# Revit family: LAMP_KOMBIC 150 ROUND IP40 OPTIC
name_source: partatom
category: Luminarias
revit_build: Autodesk Revit 2018 (Build: 20190510_1515(x64)
units: mm (PartAtom-declared; Revit-internal decimal feet)

## family parameters
Anfitrión = Cara
Compartido = No
Corte con vacíos al cargar = No
Cota de conector redondo = Diámetro de uso
Origen de luz = Sí
Punto de cálculo de habitación = No
Tipo de pieza = Normal

## types (24) — shared parameters
CRI = 80
Cambio de temperatura de color de luz atenuada = <Ninguno>
Diameter = 150 mm
Elevación por defecto = 1219 mm
Filtro de color = 16777215
Height = 100 mm  [stored 0.328084 ft]
IEE = A+
Insulation class = II
Lamp = COB LED
Luminaire type = Downlight
MacAdam = 3
Material COB = LAMP_COB
Material difusor = LAMP_PMMA Difusor Kombic
Material disipador = LAMP_Aluminio Disipador Kombic
Material optica = LAMP_PMMA Optica Kombic100
Power Supply = 220-240V 50/60Hz
Protection rating = IP40
Recessed diameter = 145 mm  [stored 0.475722 ft]
Type = COB PHILIPS
Weight = 0.69 kg
Ángulo de inclinación = -90.00°

## per-type parameters (varying)
| type | Archivo de red fotométrica | Efficacy | Fabricante | Finish | Gear | Installation instructions | LED Lifetime | Last update | Manufacturer URL | Manufacturer country | Manufacturer name | Material aro | Material reflector | Modelo | Plum | Power | Product URL | Product code | Product datasheet | UGR |
| 1145LM 3000K  B/B | K21RD2040WF830NBB.IES | 86 lm/W | LAMP | Matte black RAL 9011 | Electronic | https://www.lamp.es | 50.000 L90 B10 | 26/08/2021 | http://www.lamp.es | Spain | LAMP | LAMP_Plástico genérico NG | LAMP_PC Reflector Kombic Metalizado Negro | K21RD2040WF830NBB | 13 W | 12 W | https://www.lamp.es | K21RD2040WF830NBB | http://www.lamp.es | 16 |
| 1145LM 3000K  B/W | K21RD2040WF830NBW.IES | 86 lm/W | LAMP | Shiny white RAL 9010 | Electronic | https://www.lamp.es | 50.000 L90 B10 | 26/08/2021 | http://www.lamp.es | Spain | LAMP | LAMP_Plástico genérico BL | LAMP_PC Reflector Kombic Metalizado Negro | K21RD2040WF830NBW | 13 W | 12 W | https://www.lamp.es | K21RD2040WF830NBW | http://www.lamp.es | 16 |
| 1148LM 3000K  M/W | K21RD2040WF830NMW.IES | 86 lm/W | LAMP | Shiny white RAL 9010 | Electronic | https://www.lamp.es | 50.000 L90 B10 | 26/08/2021 | http://www.lamp.es | Spain | LAMP | LAMP_Plástico genérico BL | LAMP_PC Reflector Kombic Metalizado Mate | K21RD2040WF830NMW | 13 W | 12 W | https://www.lamp.es | K21RD2040WF830NMW | http://www.lamp.es | 16 |
| 1184LM 3000K  W/W | K21RD2040WF830NWW.IES | 88 lm/W | LAMP | Matte white RAL 9010 | Electronic | https://www.lamp.es | 50.000 L90 B10 | 26/08/2021 | http://www.lamp.es | Spain | LAMP | LAMP_Plástico genérico BL | LAMP_PC Reflector Kombic Blanco | K21RD2040WF830NWW | 13 W | 12 W | https://www.lamp.es | K21RD2040WF830NWW | http://www.lamp.es | 16 |
| 1193LM 4000K  B/B | K21RD2040WF840NBB.IES | 87 lm/W | LAMP | Matte black RAL 9011 | Electronic | https://www.lamp.es | 50.000 L90 B10 | 26/08/2021 | http://www.lamp.es | Spain | LAMP | LAMP_Plástico genérico NG | LAMP_PC Reflector Kombic Metalizado Negro | K21RD2040WF840NBB | 14 W | 12 W | https://www.lamp.es | K21RD2040WF840NBB | http://www.lamp.es | 16 |
| 1193LM 4000K  B/W | K21RD2040WF840NBW.IES | 87 lm/W | LAMP | Shiny white RAL 9010 | Electronic | https://www.lamp.es | 50.000 L90 B10 | 26/08/2021 | http://www.lamp.es | Spain | LAMP | LAMP_Plástico genérico BL | LAMP_PC Reflector Kombic Metalizado Negro | K21RD2040WF840NBW | 14 W | 12 W | https://www.lamp.es | K21RD2040WF840NBW | http://www.lamp.es | 16 |
| 1196LM 4000K  M/W | K21RD2040WF840NMW.IES | 87 lm/W | LAMP | Shiny white RAL 9010 | Electronic | https://www.lamp.es | 50.000 L90 B10 | 26/08/2021 | http://www.lamp.es | Spain | LAMP | LAMP_Plástico genérico BL | LAMP_PC Reflector Kombic Metalizado Mate | K21RD2040WF840NMW | 14 W | 12 W | https://www.lamp.es | K21RD2040WF840NMW | http://www.lamp.es | 16 |
| 1233LM 4000K  W/W | K21RD2040WF840NWW.IES | 90 lm/W | LAMP | Matte white RAL 9010 | Electronic | https://www.lamp.es | 50.000 L90 B10 | 26/08/2021 | http://www.lamp.es | Spain | LAMP | LAMP_Plástico genérico BL | LAMP_PC Reflector Kombic Blanco | K21RD2040WF840NWW | 14 W | 12 W | https://www.lamp.es | K21RD2040WF840NWW | http://www.lamp.es | 16 |
| 1613LM 3000K  B/B | K21RD3040WF830NBB.IES | 81 lm/W | LAMP | Matte black RAL 9011 | Electronic | https://www.lamp.es | 50.000 L70 B10 | 26/08/2021 | http://www.lamp.es | Spain | LAMP | LAMP_Plástico genérico NG | LAMP_PC Reflector Kombic Metalizado Negro | K21RD3040WF830NBB | 20 W | 18 W | https://www.lamp.es | K21RD3040WF830NBB | http://www.lamp.es | 19 |
| 1613LM 3000K  B/W | K21RD3040WF830NBW.IES | 81 lm/W | LAMP | Shiny white RAL 9010 | Electronic | https://www.lamp.es | 50.000 L70 B10 | 26/08/2021 | http://www.lamp.es | Spain | LAMP | LAMP_Plástico genérico BL | LAMP_PC Reflector Kombic Metalizado Negro | K21RD3040WF830NBW | 20 W | 18 W | https://www.lamp.es | K21RD3040WF830NBW | http://www.lamp.es | 19 |
| 1618LM 3000K  M/W | K21RD3040WF830NMW.IES | 81 lm/W | LAMP | Shiny white RAL 9010 | Electronic | https://www.lamp.es | 50.000 L70 B10 | 26/08/2021 | http://www.lamp.es | Spain | LAMP | LAMP_Plástico genérico BL | LAMP_PC Reflector Kombic Metalizado Mate | K21RD3040WF830NMW | 20 W | 18 W | https://www.lamp.es | K21RD3040WF830NMW | http://www.lamp.es | 19 |
| 1667LM 3000K  W/W | K21RD3040WF830NWW.IES | 84 lm/W | LAMP | Matte white RAL 9010 | Electronic | https://www.lamp.es | 50.000 L70 B10 | 26/08/2021 | http://www.lamp.es | Spain | LAMP | LAMP_Plástico genérico BL | LAMP_PC Reflector Kombic Blanco | K21RD3040WF830NWW | 20 W | 18 W | https://www.lamp.es | K21RD3040WF830NWW | http://www.lamp.es | 19 |
| 1680LM 4000K  B/B | K21RD3040WF840NBB.IES | 84 lm/W | LAMP | Matte black RAL 9011 | Electronic | https://www.lamp.es | 50.000 L70 B10 | 26/08/2021 | http://www.lamp.es | Spain | LAMP | LAMP_Plástico genérico NG | LAMP_PC Reflector Kombic Metalizado Negro | K21RD3040WF840NBB | 20 W | 18 W | https://www.lamp.es | K21RD3040WF840NBB | http://www.lamp.es | 19 |
| 1680LM 4000K  B/W | K21RD3040WF840NBW.IES | 84 lm/W | LAMP | Shiny white RAL 9010 | Electronic | https://www.lamp.es | 50.000 L70 B10 | 26/08/2021 | http://www.lamp.es | Spain | LAMP | LAMP_Plástico genérico BL | LAMP_PC Reflector Kombic Metalizado Negro | K21RD3040WF840NBW | 20 W | 18 W | https://www.lamp.es | K21RD3040WF840NBW | http://www.lamp.es | 19 |
| 1685LM 4000K  M/W | K21RD3040WF840NMW.IES | 87 lm/W | LAMP | Shiny white RAL 9010 | Electronic | https://www.lamp.es | 50.000 L70 B10 | 26/08/2021 | http://www.lamp.es | Spain | LAMP | LAMP_Plástico genérico BL | LAMP_PC Reflector Kombic Metalizado Mate | K21RD3040WF840NMW | 20 W | 18 W | https://www.lamp.es | K21RD3040WF840NMW | http://www.lamp.es | 19 |
| 1737LM 4000K  W/W | K21RD3040WF840NWW.IES | 91 lm/W | LAMP | Matte white RAL 9010 | Electronic | https://www.lamp.es | 50.000 L70 B10 | 26/08/2021 | http://www.lamp.es | Spain | LAMP | LAMP_Plástico genérico BL | LAMP_PC Reflector Kombic Blanco | K21RD3040WF840NWW | 19 W | 19 W | https://www.lamp.es | K21RD3040WF840NWW | http://www.lamp.es | 19 |
| 2145LM 3000K  B/B | K21RD3540WF830NBB.IES | 77 lm/W |  | Matte black RAL 9011 |  |  | 50.000 L70 B10 |  |  |  |  | LAMP_Plástico genérico NG | LAMP_PC Reflector Kombic Metalizado Negro | K21RD3540WF830NBB | 28 W | 25 W |  | K21RD3540WF830NBB |  | 19 |
| 2145LM 3000K  B/W | K21RD3540WF830NBW.IES | 77 lm/W |  | Shiny white RAL 9010 |  |  | 50.000 L70 B10 |  |  |  |  | LAMP_Plástico genérico BL | LAMP_PC Reflector Kombic Metalizado Negro | K21RD3540WF830NBW | 28 W | 25 W |  | K21RD3540WF830NBW |  | 19 |
| 2151LM 3000K  M/W | K21RD3540WF830NMW.IES | 78 lm/W |  | Shiny white RAL 9010 |  |  | 50.000 L70 B10 |  |  |  |  | LAMP_Plástico genérico BL | LAMP_PC Reflector Kombic Metalizado Mate | K21RD3540WF830NMW | 28 W | 25 W |  | K21RD3540WF830NMW |  | 19 |
| 2217LM 3000K  W/W | K21RD3540WF830NWW.IES | 80 lm/W |  | Matte white RAL 9010 |  |  | 50.000 L70 B10 |  |  |  |  | LAMP_Plástico genérico BL | LAMP_PC Reflector Kombic Blanco | K21RD3540WF830NWW | 28 W | 25 W |  | K21RD3540WF830NWW |  | 19 |
| 2235LM 4000K  B/B | K21RD3540WF840NBB.IES | 81 lm/W |  | Matte black RAL 9011 |  |  | 50.000 L70 B10 |  |  |  |  | LAMP_Plástico genérico NG | LAMP_PC Reflector Kombic Metalizado Negro | K21RD3540WF840NBB | 28 W | 25 W |  | K21RD3540WF840NBB |  | 19 |
| 2235LM 4000K  B/W | K21RD3540WF840NBW.IES | 81 lm/W |  | Shiny white RAL 9010 |  |  | 50.000 L70 B10 |  |  |  |  | LAMP_Plástico genérico BL | LAMP_PC Reflector Kombic Metalizado Negro | K21RD3540WF840NBW | 28 W | 25 W |  | K21RD3540WF840NBW |  | 19 |
| 2241LM 4000K  M/W | K21RD3540WF840NMW.IES | 81 lm/W |  | Shiny white RAL 9010 |  |  | 50.000 L70 B10 |  |  |  |  | LAMP_Plástico genérico BL | LAMP_PC Reflector Kombic Metalizado Mate | K21RD3540WF840NMW | 28 W | 25 W |  | K21RD3540WF840NMW |  | 19 |
| 2310LM 4000K  W/W | K21RD3540WF840NWW.IES | 83 lm/W |  | Matte white RAL 9010 |  |  | 50.000 L70 B10 |  |  |  |  | LAMP_Plástico genérico BL | LAMP_PC Reflector Kombic Blanco | K21RD3540WF840NWW | 28 W | 25 W |  | K21RD3540WF840NWW |  | 19 |

note: [stored X ft] marks values corroborated as IEEE doubles in the binary element streams (Revit-internal decimal feet)
